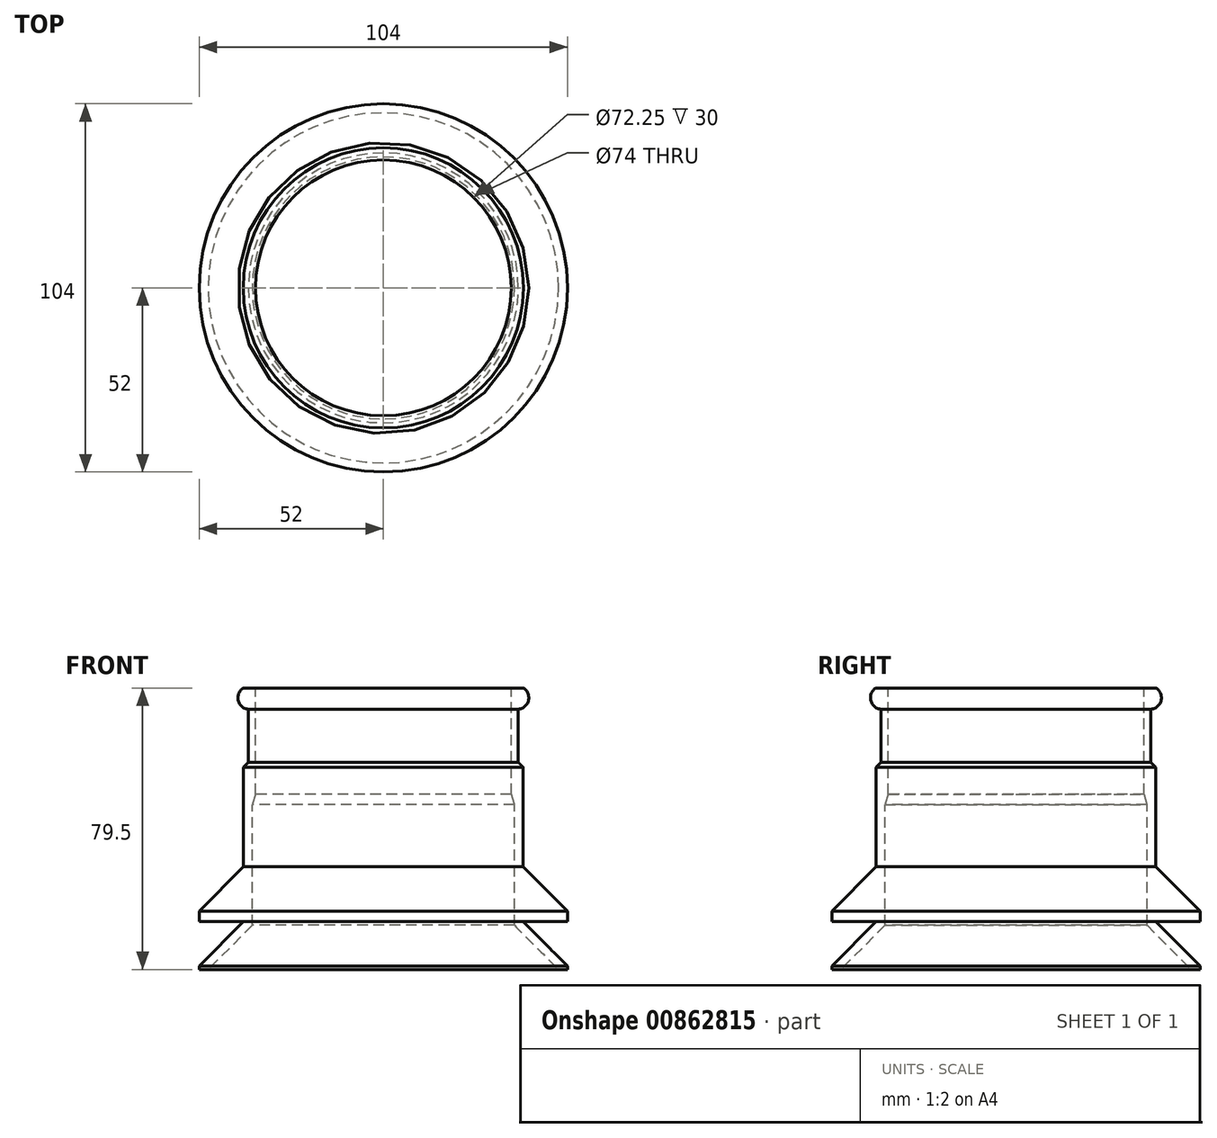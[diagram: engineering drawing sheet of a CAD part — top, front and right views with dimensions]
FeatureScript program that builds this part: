
annotation { "Feature Type Name" : "Feature", "Feature Type Description" : "" }
export const myFeature = defineFeature(function(context is Context, id is Id, definition is map)
    precondition{}
    {
        {
            var Q0;
            Q0=qCreatedBy(makeId("Front.planeOp"),FACE);
            var sketch = newSketch(context, id + "F0", { "sketchPlane" : qUnion([Q0])});
            skLineSegment(sketch, "E0", {"start": v(39.5, 0) * mm, "end": v(52, 0) * mm});
            skLineSegment(sketch, "E1", {"start": v(52, 0) * mm, "end": v(52, 3) * mm});
            skLineSegment(sketch, "E2", {"start": v(52, 3) * mm, "end": v(39.5, 3) * mm});
            skLineSegment(sketch, "E3", {"start": v(39.5, 3) * mm, "end": v(39.5, 43.63) * mm});
            skLineSegment(sketch, "E4", {"start": v(39.5, 43.63) * mm, "end": v(38.13, 45) * mm});
            skLineSegment(sketch, "E5", {"start": v(38.13, 45) * mm, "end": v(38.13, 60) * mm});
            skLineSegment(sketch, "E6", {"start": v(37, -1.04) * mm, "end": v(37, 33) * mm});
            skLineSegment(sketch, "E7", {"start": v(37, 33) * mm, "end": v(36.13, 36) * mm});
            skLineSegment(sketch, "E8", {"start": v(36.13, 36) * mm, "end": v(36.13, 66) * mm});
            skArc(sketch, "E9", {"start": v(38.13, 60) * mm, "mid": v(41, 62.49) * mm, "end": v(39.55, 66) * mm});
            skPoint(sketch, "E9.third.point", {"position": v(40.87, 64.42) * mm});
            skLineSegment(sketch, "E10", {"start": v(0, 73.13) * mm, "end": v(0, -3.93) * mm, "construction": true});
            skLineSegment(sketch, "E11.right", {"start": v(52, -13.5) * mm, "end": v(52, -12.5) * mm});
            skLineSegment(sketch, "E12", {"start": v(52, -12.5) * mm, "end": v(39.5, 0) * mm});
            skLineSegment(sketch, "E13", {"start": v(37, -1.04) * mm, "end": v(49.46, -13.5) * mm});
            skLineSegment(sketch, "E14", {"start": v(52, -13.5) * mm, "end": v(49.46, -13.5) * mm});
            skLineSegment(sketch, "E15", {"start": v(52, 3) * mm, "end": v(39.5, 15.5) * mm});
            skLineSegment(sketch, "E16", {"start": v(36.13, 66) * mm, "end": v(67.4, 66) * mm});
            skLineSegment(sketch, "E17", {"start": v(39.55, 66) * mm, "end": v(41.94, 64.52) * mm, "construction": true});
            skSolve(sketch);
        }
        {
            var Q0;
            {var subQ0=sQuery(id+"F0.wireOp",EDGE,"E9");var subQ1=sQuery(id+"F0.wireOp",EDGE,"E8");var subQ2=makeQuery(id+"F0.imprint","INTERSECT",VERTEX,{"disambiguationData":[OD(0.0)],"derivedFrom":[subQ1,subQ0]});Q0=makeQuery(id+"F0.imprint","IMPRINT",FACE,{"disambiguationData":[TD([[makeQuery(id+"F0.imprint","IMPRINT",EDGE,{"disambiguationData":[TD([[subQ2,1.0]])],"derivedFrom":subQ1}),-1.0]])]});}
            var Q1;
            Q1=makeQuery(id+"F0.imprint","IMPRINT",FACE,{"disambiguationData":[TD([[makeQuery(id+"F0.imprint","IMPRINT",EDGE,{"derivedFrom":sQuery(id+"F0.wireOp",EDGE,"E0")}),1.0]])]});
            var Q2;
            {var subQ0=sQuery(id+"F0.wireOp",EDGE,"qJt6J9Uv-qvfz-0X9m-ZeLu-DlGv1RXLZgkY");Q2=makeQuery(id+"F0.imprint","IMPRINT",FACE,{"disambiguationData":[TD([[makeQuery(id+"F0.imprint","IMPRINT",EDGE,{"derivedFrom":subQ0}),1.0]])]});}
            var Q3;
            {var subQ0=sQuery(id+"F0.wireOp",EDGE,"E2");Q3=makeQuery(id+"F0.imprint","IMPRINT",FACE,{"disambiguationData":[TD([[makeQuery(id+"F0.imprint","IMPRINT",EDGE,{"derivedFrom":subQ0}),-1.0]])]});}
            var Q4;
            Q4=sQuery(id+"F0.wireOp",EDGE,"E10");
            revolve(context, id + "F1", {"surfaceOperationType" : NewSurfaceOperationType.NEW, "entities" : qUnion([Q0, Q1, Q2, Q3]), "axis" : qUnion([Q4]), "revolveType" : RevolveType.FULL});
        }
    });
